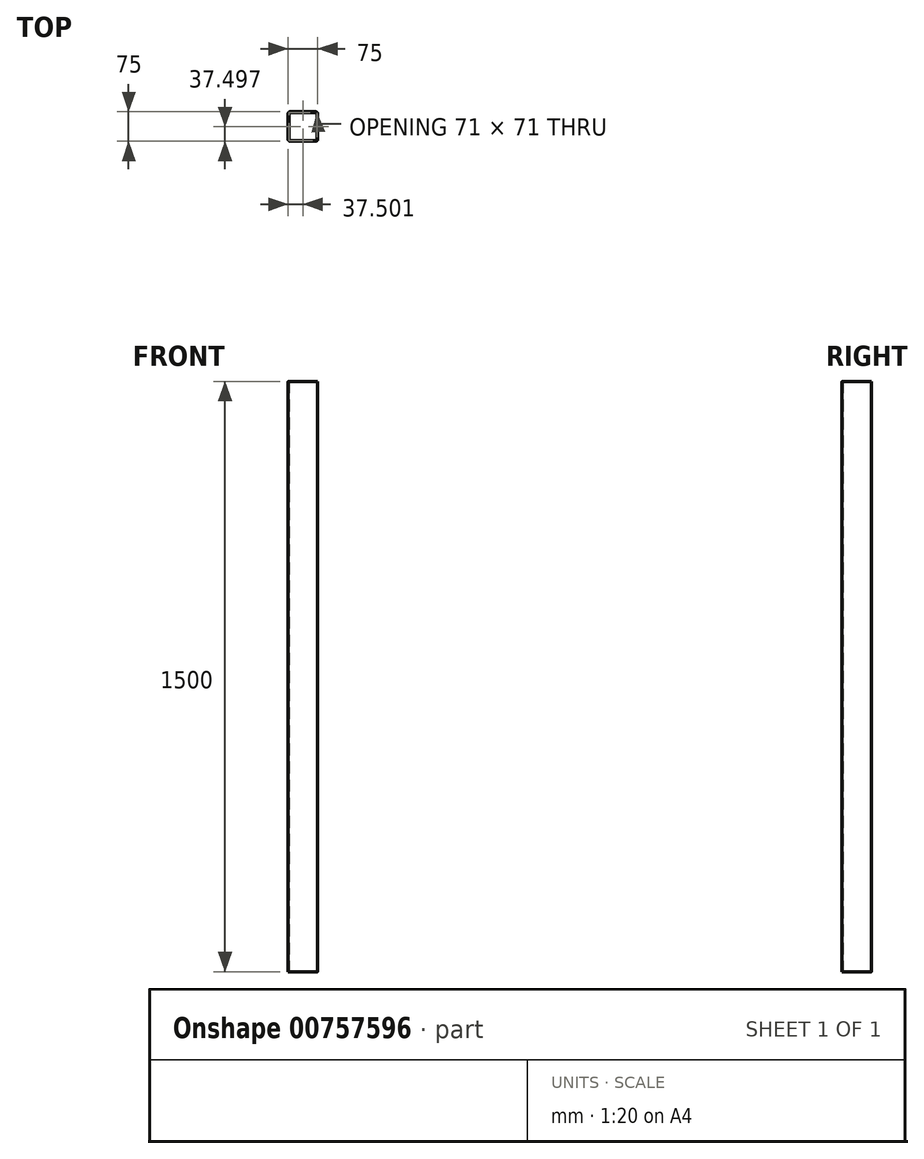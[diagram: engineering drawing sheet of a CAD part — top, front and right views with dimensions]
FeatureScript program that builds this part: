
annotation { "Feature Type Name" : "Feature", "Feature Type Description" : "" }
export const myFeature = defineFeature(function(context is Context, id is Id, definition is map)
    precondition{}
    {
        {
            var Q0;
            Q0=qCreatedBy(makeId("Top.planeOp"),FACE);
            var sketch = newSketch(context, id + "F0", { "sketchPlane" : qUnion([Q0])});
            skLineSegment(sketch, "E0.bottom", {"start": v(-33.59, 33.8) * mm, "end": v(31.41, 33.8) * mm});
            skLineSegment(sketch, "E0.top", {"start": v(-33.59, -41.2) * mm, "end": v(31.41, -41.2) * mm});
            skLineSegment(sketch, "E0.left", {"start": v(-38.59, 28.8) * mm, "end": v(-38.59, -36.2) * mm});
            skLineSegment(sketch, "E0.right", {"start": v(36.41, 28.8) * mm, "end": v(36.41, -36.2) * mm});
            skPoint(sketch, "E1.visualSharp", {"position": v(-38.59, 33.8) * mm});
            skArc(sketch, "E1.filletArc", {"start": v(-33.59, 33.8) * mm, "mid": v(-37.12, 32.33) * mm, "end": v(-38.59, 28.8) * mm});
            skPoint(sketch, "E2.visualSharp", {"position": v(36.41, 33.8) * mm});
            skArc(sketch, "E2.filletArc", {"start": v(36.41, 28.8) * mm, "mid": v(34.95, 32.33) * mm, "end": v(31.41, 33.8) * mm});
            skPoint(sketch, "E3.visualSharp", {"position": v(36.41, -41.2) * mm});
            skArc(sketch, "E3.filletArc", {"start": v(31.41, -41.2) * mm, "mid": v(34.95, -39.74) * mm, "end": v(36.41, -36.2) * mm});
            skPoint(sketch, "E4.visualSharp", {"position": v(-38.59, -41.2) * mm});
            skArc(sketch, "E4.filletArc", {"start": v(-38.59, -36.2) * mm, "mid": v(-37.12, -39.74) * mm, "end": v(-33.59, -41.2) * mm});
            skLineSegment(sketch, "E5.0", {"start": v(-33.59, -39.2) * mm, "end": v(31.41, -39.2) * mm});
            skLineSegment(sketch, "E5.1", {"start": v(-36.59, 28.8) * mm, "end": v(-36.59, -36.2) * mm});
            skLineSegment(sketch, "E5.2", {"start": v(-33.59, 31.8) * mm, "end": v(31.41, 31.8) * mm});
            skLineSegment(sketch, "E5.3", {"start": v(34.41, 28.8) * mm, "end": v(34.41, -36.2) * mm});
            skPoint(sketch, "E6.visualSharp", {"position": v(-36.59, -39.2) * mm});
            skArc(sketch, "E6.filletArc", {"start": v(-36.59, -36.2) * mm, "mid": v(-35.71, -38.32) * mm, "end": v(-33.59, -39.2) * mm});
            skPoint(sketch, "E7.visualSharp", {"position": v(34.41, 31.8) * mm});
            skArc(sketch, "E7.filletArc", {"start": v(34.41, 28.8) * mm, "mid": v(33.53, 30.92) * mm, "end": v(31.41, 31.8) * mm});
            skPoint(sketch, "E8.visualSharp", {"position": v(-36.59, 31.8) * mm});
            skArc(sketch, "E8.filletArc", {"start": v(-33.59, 31.8) * mm, "mid": v(-35.71, 30.92) * mm, "end": v(-36.59, 28.8) * mm});
            skPoint(sketch, "E9.visualSharp", {"position": v(34.41, -39.2) * mm});
            skArc(sketch, "E9.filletArc", {"start": v(31.41, -39.2) * mm, "mid": v(33.53, -38.32) * mm, "end": v(34.41, -36.2) * mm});
            skSolve(sketch);
        }
        {
            var Q0;
            Q0=qSketchRegion(id+"F0",true);
            extrude(context, id + "F1", {"entities" : qUnion([Q0]), "depth" : 1500 * mm, "offsetDistance" : 25 * mm});
        }
    });
